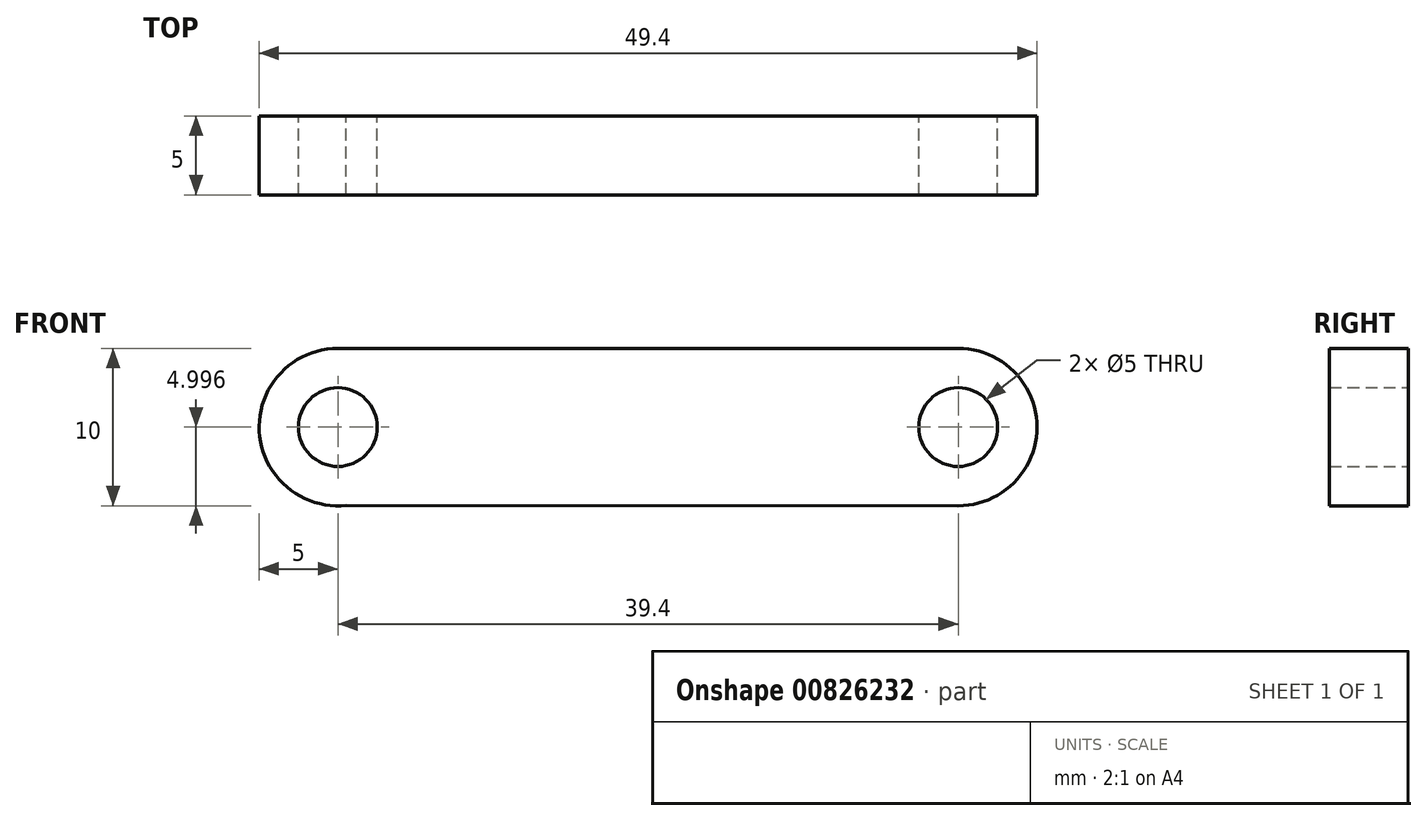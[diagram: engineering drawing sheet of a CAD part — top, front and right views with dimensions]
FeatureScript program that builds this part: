
annotation { "Feature Type Name" : "Feature", "Feature Type Description" : "" }
export const myFeature = defineFeature(function(context is Context, id is Id, definition is map)
    precondition{}
    {
        {
            var Q0;
            Q0=qCreatedBy(makeId("Front.planeOp"),FACE);
            var sketch = newSketch(context, id + "F0", { "sketchPlane" : qUnion([Q0])});
            skArc(sketch, "E0", {"start": v(-14.81, 14.08) * mm, "mid": v(-19.8, 8.8) * mm, "end": v(-14.28, 4.1) * mm});
            skArc(sketch, "E1", {"start": v(24.59, 4.08) * mm, "mid": v(29.59, 9.07) * mm, "end": v(24.59, 14.08) * mm});
            skLineSegment(sketch, "E2", {"start": v(-14.81, 14.08) * mm, "end": v(24.59, 14.08) * mm});
            skLineSegment(sketch, "E3", {"start": v(-14.28, 4.1) * mm, "end": v(24.59, 4.08) * mm});
            skCircle(sketch, "E4", {"center": v(-14.81, 9.08) * mm, "radius": 2.5 * mm});
            skCircle(sketch, "E5", {"center": v(24.59, 9.08) * mm, "radius": 2.5 * mm});
            skSolve(sketch);
        }
        {
            var Q0;
            Q0 = qSketchRegion(id + "F0", true);
            extrude(context, id + "F1", {"entities" : qUnion([Q0]), "depth" : 5 * mm, "offsetDistance" : 25 * mm});
        }
    });
